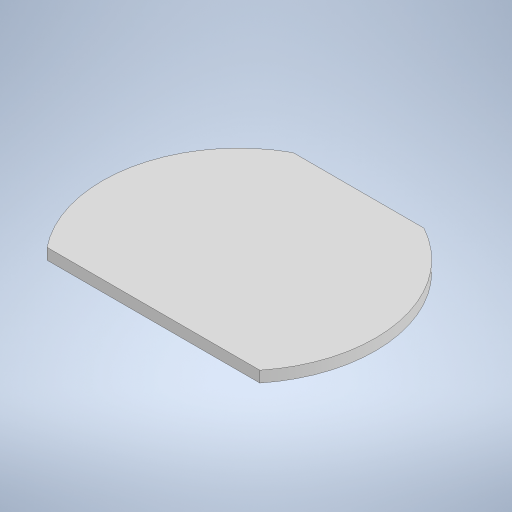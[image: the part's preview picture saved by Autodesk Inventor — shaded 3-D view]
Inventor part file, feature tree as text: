
AUTODESK INVENTOR PART (.ipt)
format: ipt  version: 2024 (Build 280153000, 153)  size: 214,016 bytes
history: native  units: mm
features: sketch x2, other x1, extrude x1, mirror x1
ambient origin geometry x8: Origin, YZ Plane, XZ Plane, XY Plane, X Axis, Y Axis, Z Axis, Center Point
bodies: Body1 (feature_tree)
feature tree (5):
  other  "ソリッド1"
  sketch  "スケッチ1"
  extrude  "押し出し1"  Depth=21.5mm
  mirror  "ミラー1"
  sketch  "スケッチ2"
